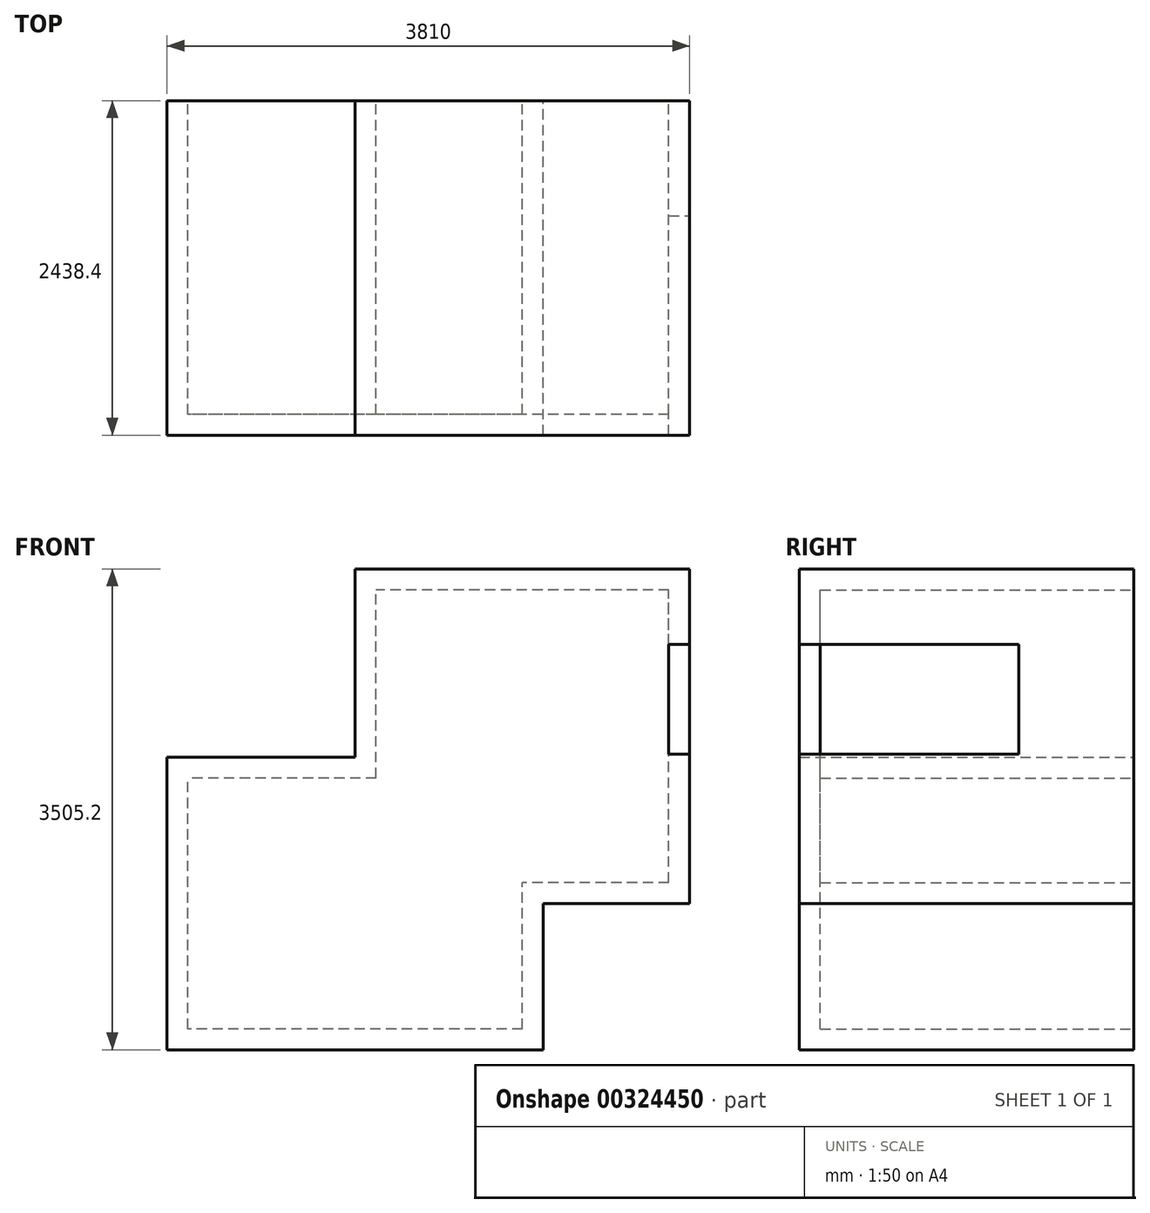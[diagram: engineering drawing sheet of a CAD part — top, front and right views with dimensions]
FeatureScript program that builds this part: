
annotation { "Feature Type Name" : "Feature", "Feature Type Description" : "" }
export const myFeature = defineFeature(function(context is Context, id is Id, definition is map)
    precondition{}
    {
        {
            var Q0;
            Q0=qCreatedBy(makeId("Front.planeOp"),FACE);
            var sketch = newSketch(context, id + "F0", { "sketchPlane" : qUnion([Q0])});
            skLineSegment(sketch, "E0.bottom", {"start": v(1219.2, -1219.2) * mm, "end": v(152.4, -1219.2) * mm});
            skLineSegment(sketch, "E0.top", {"start": v(1219.2, 1219.2) * mm, "end": v(-1219.2, 1219.2) * mm});
            skLineSegment(sketch, "E0.left", {"start": v(1219.2, -1219.2) * mm, "end": v(1219.2, 1219.2) * mm});
            skLineSegment(sketch, "E0.right", {"start": v(-1219.2, -152.4) * mm, "end": v(-1219.2, 1219.2) * mm});
            skPoint(sketch, "E0.middle", {"position": v(0, 0) * mm});
            skLineSegment(sketch, "E1.bottom", {"start": v(152.4, -2286) * mm, "end": v(-2590.8, -2286) * mm});
            skLineSegment(sketch, "E1.top", {"start": v(-1219.2, -152.4) * mm, "end": v(-2590.8, -152.4) * mm});
            skLineSegment(sketch, "E1.left", {"start": v(152.4, -2286) * mm, "end": v(152.4, -1219.2) * mm});
            skLineSegment(sketch, "E1.right", {"start": v(-2590.8, -2286) * mm, "end": v(-2590.8, -152.4) * mm});
            skPoint(sketch, "E2", {"position": v(-1219.2, -152.4) * mm});
            skPoint(sketch, "E3", {"position": v(152.4, -1219.2) * mm});
            skSolve(sketch);
        }
        {
            var Q0;
            Q0=makeQuery(id+"F0.imprint","IMPRINT",FACE,{"disambiguationData":[TD([[makeQuery(id+"F0.imprint","IMPRINT",EDGE,{"derivedFrom":sQuery(id+"F0.wireOp",EDGE,"E0.bottom")}),-1.0]])]});
            extrude(context, id + "F1", {"entities" : qUnion([Q0]), "depth" : 2438.4 * mm});
        }
        {
            var Q0;
            Q0=makeQuery(id+"F1.opExtrude","CAP_FACE",FACE,{"disambiguationData":[OSD([sQuery(id+"F0.wireOp",EDGE,"E0.bottom"),sQuery(id+"F0.wireOp",EDGE,"E0.top"),sQuery(id+"F0.wireOp",EDGE,"E0.left"),sQuery(id+"F0.wireOp",EDGE,"E0.right"),sQuery(id+"F0.wireOp",EDGE,"E1.bottom"),sQuery(id+"F0.wireOp",EDGE,"E1.top"),sQuery(id+"F0.wireOp",EDGE,"E1.left"),sQuery(id+"F0.wireOp",EDGE,"E1.right")])],"isStart":true});
            shell(context, id + "F2", {"entities" : qUnion([Q0]), "thickness" : 152.4 * mm});
        }
        {
            var Q0;
            Q0=makeQuery(id+"F1.opExtrude","SWEPT_FACE",FACE,{"disambiguationData":[OSD([sQuery(id+"F0.wireOp",EDGE,"E0.left")])]});
            var sketch = newSketch(context, id + "F3", { "sketchPlane" : qUnion([Q0])});
            skLineSegment(sketch, "E4.bottom", {"start": v(-2438.4, 668.76) * mm, "end": v(-839.14, 668.76) * mm});
            skLineSegment(sketch, "E4.top", {"start": v(-2438.4, -130.8) * mm, "end": v(-839.14, -130.8) * mm});
            skLineSegment(sketch, "E4.left", {"start": v(-2438.4, 668.76) * mm, "end": v(-2438.4, -130.8) * mm});
            skLineSegment(sketch, "E4.right", {"start": v(-839.14, 668.76) * mm, "end": v(-839.14, -130.8) * mm});
            skSolve(sketch);
        }
        {
            var Q0;
            Q0=makeQuery(id+"F3.imprint","IMPRINT",FACE,{"disambiguationData":[TD([[makeQuery(id+"F3.imprint","IMPRINT",EDGE,{"derivedFrom":sQuery(id+"F3.wireOp",EDGE,"E4.bottom")}),-1.0]])]});
            extrude(context, id + "F4", {"entities" : qUnion([Q0]), "operationType" : NewBodyOperationType.REMOVE, "oppositeDirection" : true, "depth" : 152.4 * mm});
        }
    });
